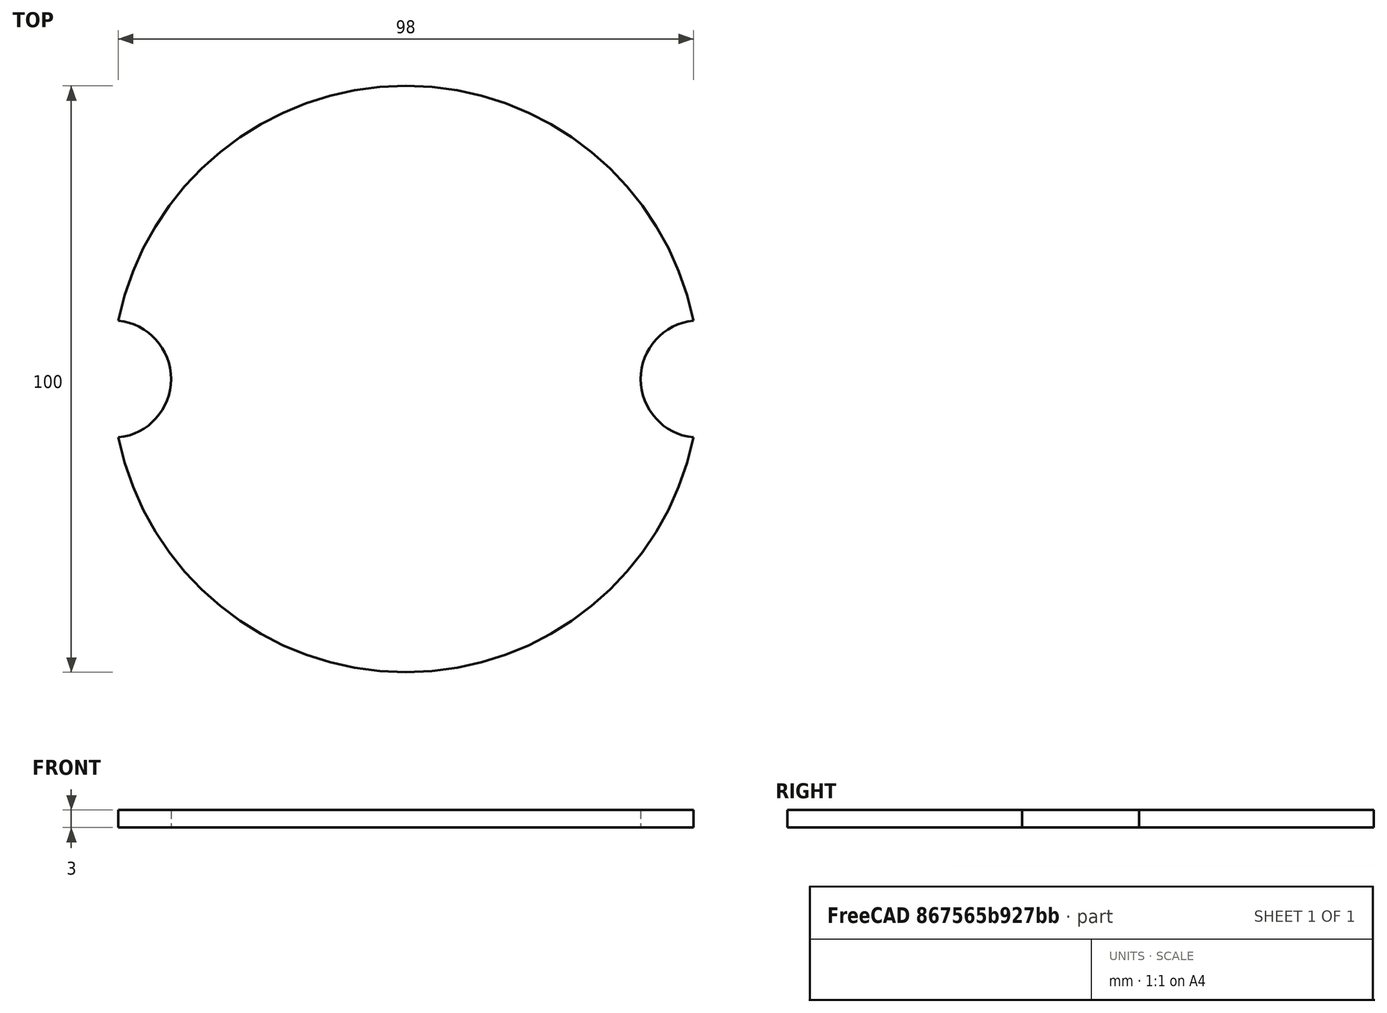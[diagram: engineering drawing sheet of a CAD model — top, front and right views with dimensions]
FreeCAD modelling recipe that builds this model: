
FCSTD DOCUMENT  (FreeCAD 0.19R24291 (Git))
Label: Coiffe-Top-Lidar
License: All rights reserved
LicenseURL: http://en.wikipedia.org/wiki/All_rights_reserved
objects: Sketcher::SketchObject×1, PartDesign::Pad×1, PartDesign::Body×1
note: 4 computed .brp shape members not serialized (recipe doc carries the construction recipe); baked Part::Feature solids carry a one-line shape summary decoded from their .brp

FEATURE [Sketcher::SketchObject] Sketch
  FullyConstrained = true
  MapMode = 5
  Support = -> [XY_Plane]
  sketch-geometry (7):
    g0: GeomPoint X=-50 Y=0 Z=0
    g1: ArcOfCircle CenterX=-50 CenterY=0 CenterZ=0 NormalX=0 NormalY=0 NormalZ=1 AngleXU=0 Radius=10 StartAngle=4.81256 EndAngle=7.75381
    g2: ArcOfCircle CenterX=50 CenterY=0 CenterZ=0 NormalX=0 NormalY=0 NormalZ=1 AngleXU=0 Radius=10 StartAngle=1.67096 EndAngle=4.61222
    g3: ArcOfCircle CenterX=0 CenterY=0 CenterZ=0 NormalX=0 NormalY=0 NormalZ=1 AngleXU=0 Radius=50 StartAngle=0.200335 EndAngle=2.94126
    g4: ArcOfCircle CenterX=0 CenterY=0 CenterZ=0 NormalX=0 NormalY=0 NormalZ=1 AngleXU=0 Radius=50 StartAngle=3.34193 EndAngle=6.08285
    g5: ArcOfCircle CenterX=0 CenterY=0 CenterZ=0 NormalX=0 NormalY=0 NormalZ=1 AngleXU=0 Radius=50 StartAngle=2.94126 EndAngle=3.34193
    g6: ArcOfCircle CenterX=0 CenterY=0 CenterZ=0 NormalX=0 NormalY=0 NormalZ=1 AngleXU=0 Radius=50 StartAngle=6.08285 EndAngle=6.48352
  constraints (20):
    c: PointOnObject(g0,g-1)
    c: Coincident(g1,g0)
    c: Radius(g1) = 10
    c: PointOnObject(g2,g-1)
    c: Coincident(g3,g-1)
    c: Coincident(g3,g1)
    c: Coincident(g3,g2)
    c: Coincident(g4,g3)
    c: Coincident(g4,g2)
    c: Coincident(g4,g1)
    c: Radius(g3) = 50
    c: Coincident(g5,g3)
    c: Coincident(g5,g1)
    c: Coincident(g5,g1)
    c: Coincident(g6,g3)
    c: Coincident(g6,g2)
    c: Coincident(g6,g2)
    c: PointOnObject(g1,g5)
    c: PointOnObject(g2,g6)
    c: Equal(g1,g2)
FEATURE [PartDesign::Pad] Pad
  Direction = (1,1,1)
  Length = 3
  Length2 = 100
  Profile = -> Sketch
  Type = 0
FEATURE [PartDesign::Body] Body
  Group = -> [Sketch,Pad]
  Origin = -> Origin
  Tip = -> Pad
